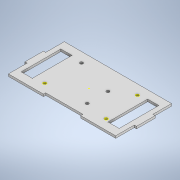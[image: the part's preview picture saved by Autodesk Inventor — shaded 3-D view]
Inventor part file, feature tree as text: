
AUTODESK INVENTOR PART (.ipt)
format: ipt  version: 2020 (Build 240168000, 168)  size: 216,576 bytes
history: native  units: in
note: dims shown in document units (in); Inventor stores cm internally (conversion verified against a paired STEP export)
features: sketch x10, extrude x7
ambient origin geometry x8: Origin, YZ Plane, XZ Plane, XY Plane, X Axis, Y Axis, Z Axis, Center Point
bodies: Solid1 (feature_tree)
feature tree (17):
  extrude  "Extrusion1"  Depth=1.9685in
  extrude  "Extrusion2"  Depth=0.1181in TaperAngle=0.0deg
  extrude  "Extrusion3"  Depth=0.1575in
  extrude  "Extrusion4"  Depth=0.1575in
  extrude  "Extrusion5"  Depth=0.3937in TaperAngle=0.0deg
  sketch  "Sketch6"  dims[d46=0.1181in d47=0.0in d61=0.1575in]
  extrude  "Extrusion6"  Depth=0.1181in
  sketch  "Sketch8"  dims[d71=0.1575in]
  sketch  "Sketch9"  dims[d74=0.1575in]
  extrude  "Extrusion7"  Depth=0.1575in
  sketch  "Sketch1"  dims[d9=0.1181in d10=0.0in d13=1.9685in]
  sketch  "Sketch2"  dims[d14=0.1181in d17=1.1811in d18=0.0in]
  sketch  "Sketch3"  dims[d32=0.1575in d35=0.1575in]
  sketch  "Sketch4"  dims[d38=0.1575in d39=0.1575in]
  sketch  "Sketch5"  dims[d42=0.3937in d43=0.0in d44=0.2062in d45=0.0in]
  sketch  "Sketch7"  dims[d63=0.1575in d69=0.1575in]
  sketch  "Sketch10"  dims[d76=0.1575in d77=0.1181in d78=0.0in d79=0.1969in d80=0.1969in d81=0.3937in d82=0.0in]
